# Revit family: Electronics_Desono_Biamp_Two-Way-Ceiling-Loudspeaker_CM60DTD
name_source: partatom
category: Communication Devices
units: mm (PartAtom-declared; Revit-internal decimal feet)

## family parameters
Cut with Voids When Loaded = No
Host = Face
Maintain Annotation Orientation = No
OmniClass Number = 23.85.10.11.14.14.14
OmniClass Title = Loudspeakers
Part Type = Normal
Room Calculation Point = No
Round Connector Dimension = Use Diameter
Shared = No

## types (1)
- CM60DTD
    Compliance = ETL listed to comply with UL 1480A and UL 2043;Certifed to CSA C22.2#62368-1;Suitable for use in air handling spaces per NFPA 70, NFPA 90;Conforms with City of Chicago Codes
    Connector Description = 4-way Euroblock; Low impedance 16 ohms, 70/100V operation
    Continuous Power Handling Nominal Impedance = 31V 60W @ 16Ω (240W peak)
    Cutout Diameter = 9.1 (232 mm)
    Default Elevation = 4' - 0"
    Depth = 0' - 6"
    Description = Desono™ CM60DTD Two-Way 6.5 Ceiling Loudspeaker
    Diameter = 0' - 10"
    Grill Material = Biamp - Plastic - Gray(Grid)
    Housing Material = Biamp - Plastic - Gray
    Input Connection = (1) 4-way Euroblock connector with permanent pass-through
    Manufacturer = Biamp
    Model = CM60DTD
    Mounting Provisions = 2 mounting clamps with grip range of 0.2 - 2.6 (3 - 65 mm);Cover plate with 0.75 (22 mm) NPT knockout for conduit connectors
    Nominal Beamwidth  (H x V) = 150° conical
    Nominal Maximum SPL @ 1m = Peak - 110dB; Continuous - 104dB
    Nominal Sensitivity @ 1m = 1W - 86dB;2.83V - 83dB
    Operating Environment = Indoor
    Operating Mode = Passive
    Operating Range (-10dB) = 75 Hz to 22 kHz
    Product Documentation Link = https://downloads.biamp.com
    Product Page URL = https://www.biamp.com
    Product data url = https://www.bimobject.com
    Protection = 3-step self-resetting protection
    Recommended Amplifers = 60W - 120W @ 16Ω (31V - 44V)
    Safety Features = 2 hang points
    Shipping Weight = 11.60 lb
    Transducers = LF 1 x 6.5 (165 mm) coated paper cone; HF 1 x 1 (25 mm) soft dome
    Transformer = 70V: 60W, 30W, 15W, 7.5W, 3.75W; 100V: 60W, 30W, 15W, 7.5W
    URL = https://www.biamp.com
    Weight = 8.80 lb

## geometry (parser evidence)
native form markers: Sweep x11
no freeform markers — native parametric forms only
